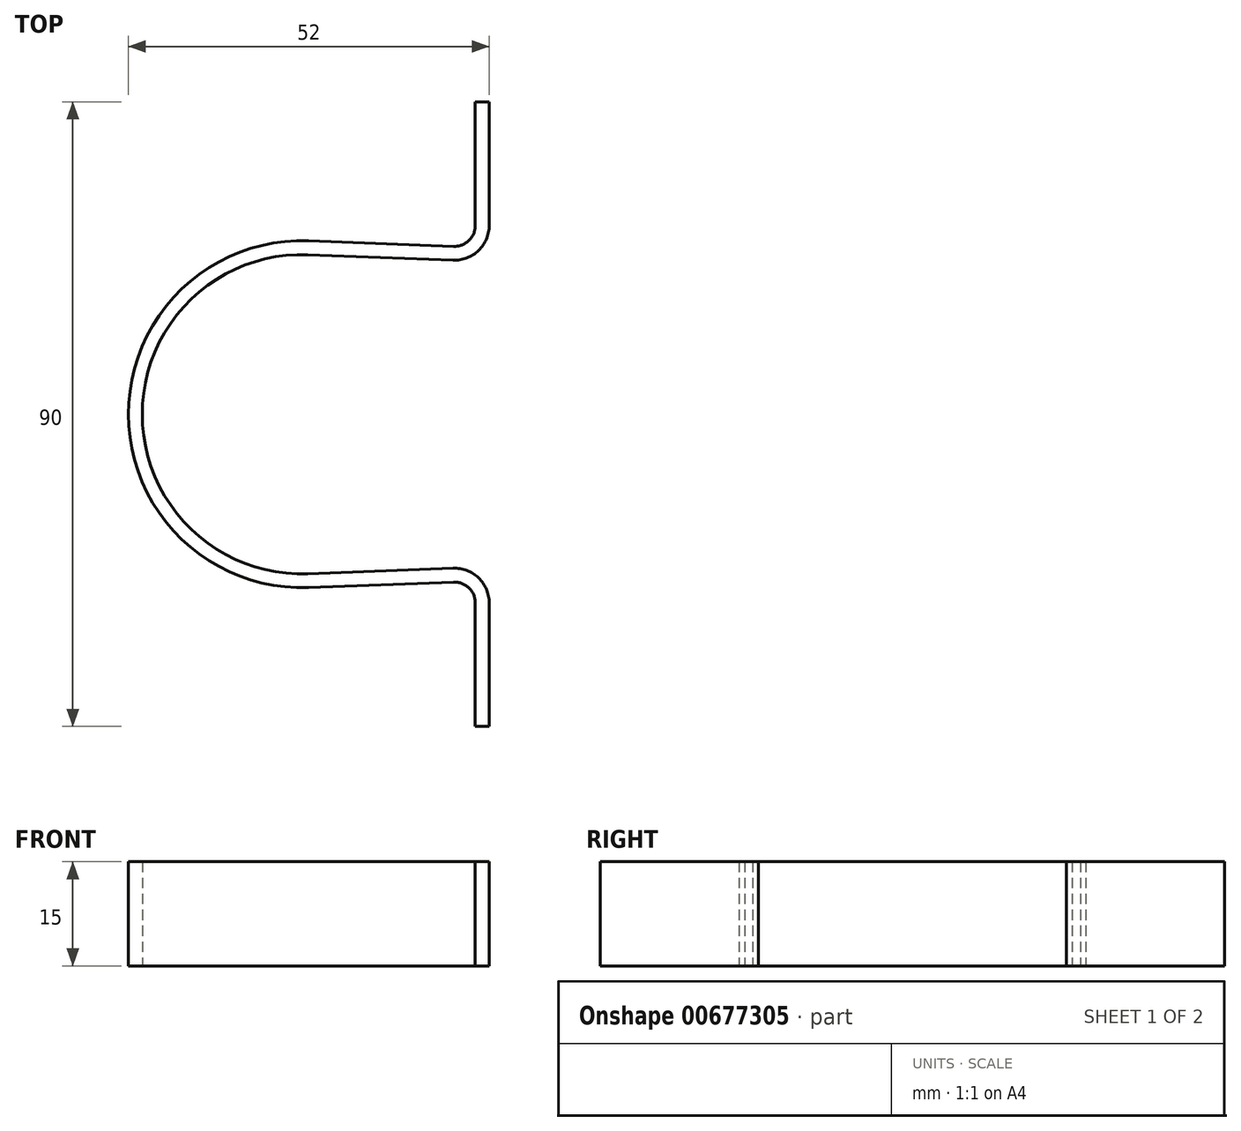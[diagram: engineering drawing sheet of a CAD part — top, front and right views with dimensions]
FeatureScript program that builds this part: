
annotation { "Feature Type Name" : "Feature", "Feature Type Description" : "" }
export const myFeature = defineFeature(function(context is Context, id is Id, definition is map)
    precondition{}
    {
        {
            var Q0;
            Q0=qCreatedBy(makeId("Top.planeOp"),FACE);
            var sketch = newSketch(context, id + "F0", { "sketchPlane" : qUnion([Q0])});
            skArc(sketch, "E0", {"start": v(0.87, 22.98) * mm, "mid": v(-23, 0) * mm, "end": v(0.87, -22.98) * mm});
            skLineSegment(sketch, "E1", {"start": v(27, 45) * mm, "end": v(27, 27.2) * mm});
            skLineSegment(sketch, "E2", {"start": v(21.81, 22.2) * mm, "end": v(0.87, 22.98) * mm});
            skLineSegment(sketch, "E3.MirrorCS", {"start": v(21.81, -22.2) * mm, "end": v(0.87, -22.98) * mm});
            skPoint(sketch, "E4", {"position": v(-23, 0) * mm});
            skLineSegment(sketch, "E5.trimOffspring", {"start": v(27, -27.2) * mm, "end": v(27, -45) * mm});
            skPoint(sketch, "E6.visualSharp", {"position": v(27, 22) * mm});
            skArc(sketch, "E6.filletArc", {"start": v(21.81, 22.2) * mm, "mid": v(25.47, 23.6) * mm, "end": v(27, 27.2) * mm});
            skPoint(sketch, "E7.visualSharp", {"position": v(27, -22) * mm});
            skArc(sketch, "E7.filletArc", {"start": v(27, -27.2) * mm, "mid": v(25.47, -23.6) * mm, "end": v(21.81, -22.2) * mm});
            skLineSegment(sketch, "E8.0", {"start": v(25, -27.2) * mm, "end": v(25, -45) * mm});
            skLineSegment(sketch, "E8.1", {"start": v(25, 45) * mm, "end": v(25, 27.2) * mm});
            skLineSegment(sketch, "E8.2", {"start": v(21.89, 24.2) * mm, "end": v(0.94, 24.98) * mm});
            skArc(sketch, "E8.3", {"start": v(0.94, 24.98) * mm, "mid": v(-25, 0) * mm, "end": v(0.94, -24.98) * mm});
            skLineSegment(sketch, "E8.4", {"start": v(21.89, -24.2) * mm, "end": v(0.94, -24.98) * mm});
            skArc(sketch, "E9.0", {"start": v(21.89, 24.2) * mm, "mid": v(24.08, 25.03) * mm, "end": v(25, 27.2) * mm});
            skArc(sketch, "E10.0", {"start": v(25, -27.2) * mm, "mid": v(24.08, -25.03) * mm, "end": v(21.89, -24.2) * mm});
            skLineSegment(sketch, "E11", {"start": v(27, 45) * mm, "end": v(25, 45) * mm});
            skLineSegment(sketch, "E12", {"start": v(27, -45) * mm, "end": v(25, -45) * mm});
            skSolve(sketch);
        }
        {
            var Q0;
            Q0=makeQuery(id+"F0.imprint","IMPRINT",FACE,{"disambiguationData":[TD([[makeQuery(id+"F0.imprint","IMPRINT",EDGE,{"derivedFrom":sQuery(id+"F0.wireOp",EDGE,"E0")}),-1.0]])]});
            extrude(context, id + "F1", {"entities" : qUnion([Q0]), "depth" : 15 * mm, "offsetDistance" : 25 * mm});
        }
    });
